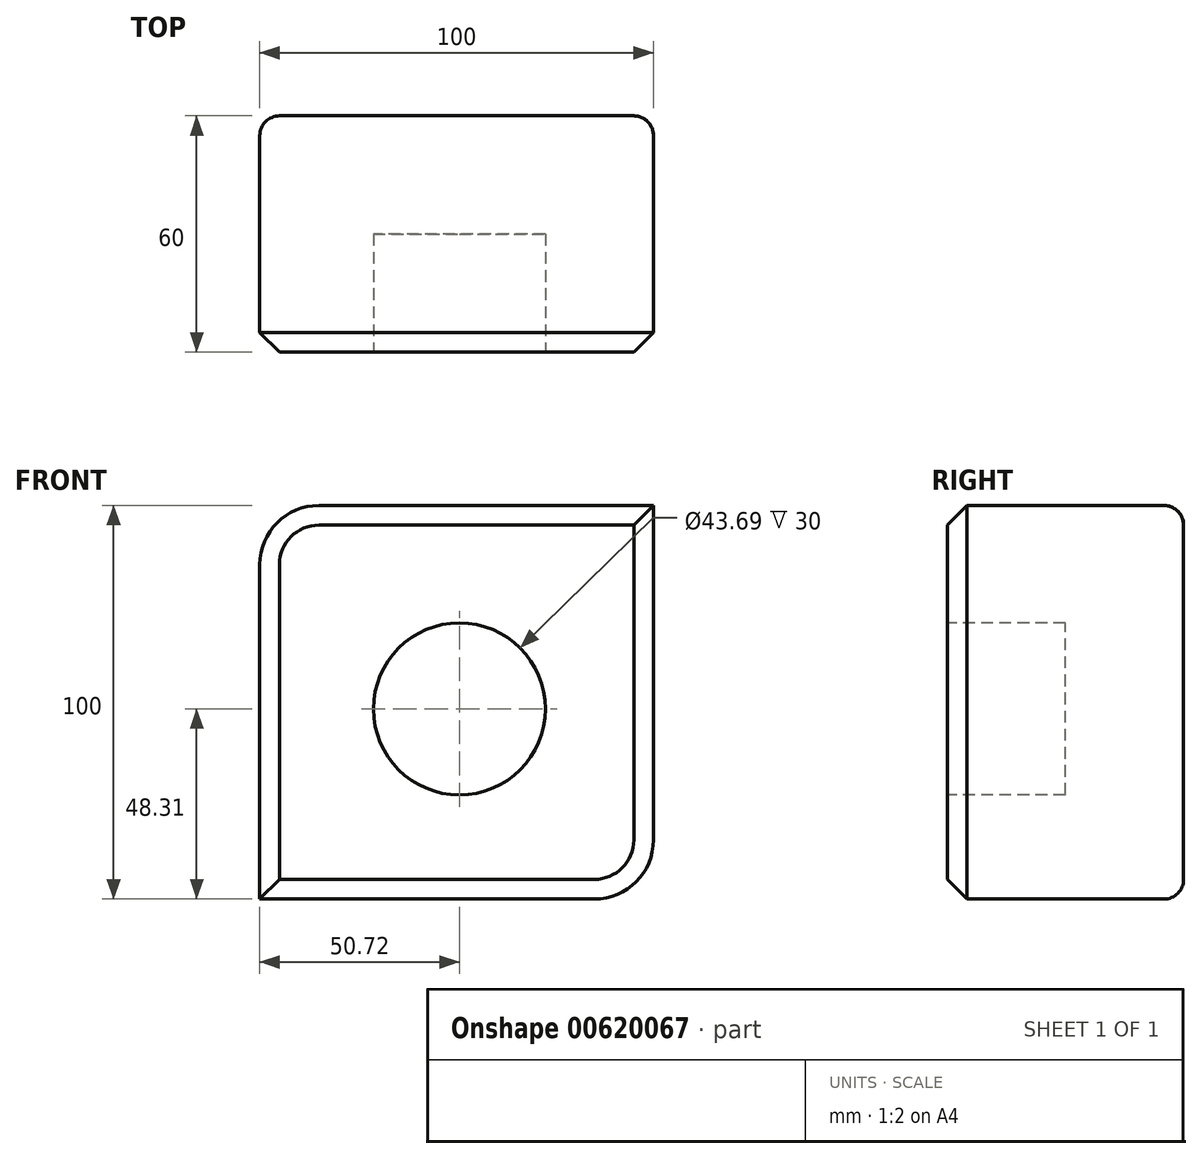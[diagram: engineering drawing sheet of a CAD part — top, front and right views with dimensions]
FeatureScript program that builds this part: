
annotation { "Feature Type Name" : "Feature", "Feature Type Description" : "" }
export const myFeature = defineFeature(function(context is Context, id is Id, definition is map)
    precondition{}
    {
        {
            var Q0;
            Q0=qCreatedBy(makeId("Front.planeOp"),FACE);
            var sketch = newSketch(context, id + "F0", { "sketchPlane" : qUnion([Q0])});
            skLineSegment(sketch, "E0.bottom", {"start": v(-35.72, 51.7) * mm, "end": v(49.28, 51.7) * mm});
            skLineSegment(sketch, "E0.top", {"start": v(-50.72, -48.3) * mm, "end": v(34.28, -48.3) * mm});
            skLineSegment(sketch, "E0.left", {"start": v(-50.72, 36.7) * mm, "end": v(-50.72, -48.3) * mm});
            skLineSegment(sketch, "E0.right", {"start": v(49.28, 51.7) * mm, "end": v(49.28, -33.3) * mm});
            skPoint(sketch, "E1.visualSharp", {"position": v(-50.72, 51.7) * mm});
            skArc(sketch, "E1.filletArc", {"start": v(-35.72, 51.7) * mm, "mid": v(-46.32, 47.3) * mm, "end": v(-50.72, 36.7) * mm});
            skPoint(sketch, "E2.visualSharp", {"position": v(49.28, -48.3) * mm});
            skArc(sketch, "E2.filletArc", {"start": v(34.28, -48.3) * mm, "mid": v(44.89, -43.91) * mm, "end": v(49.28, -33.3) * mm});
            skSolve(sketch);
        }
        {
            var Q0;
            Q0 = qSketchRegion(id + "F0", true);
            extrude(context, id + "F1", {"entities" : qUnion([Q0]), "depth" : 60 * mm, "offsetDistance" : 25 * mm});
        }
        {
            var Q0;
            Q0=makeQuery(id+"F1.opExtrude","CAP_FACE",FACE,{"disambiguationData":[OSD([sQuery(id+"F0.wireOp",EDGE,"E0.bottom"),sQuery(id+"F0.wireOp",EDGE,"E0.top"),sQuery(id+"F0.wireOp",EDGE,"E0.left"),sQuery(id+"F0.wireOp",EDGE,"E0.right"),sQuery(id+"F0.wireOp",EDGE,"E1.filletArc"),sQuery(id+"F0.wireOp",EDGE,"E2.filletArc")])],"isStart":true});
            fillet(context, id + "F2", {"entities" : qUnion([Q0]), "radius" : 5 * mm, "tangentPropagation" : true, "allowEdgeOverflow" : false});
        }
        {
            var Q0;
            Q0=makeQuery(id+"F1.opExtrude","CAP_FACE",FACE,{"disambiguationData":[OSD([sQuery(id+"F0.wireOp",EDGE,"E0.bottom"),sQuery(id+"F0.wireOp",EDGE,"E0.top"),sQuery(id+"F0.wireOp",EDGE,"E0.left"),sQuery(id+"F0.wireOp",EDGE,"E0.right"),sQuery(id+"F0.wireOp",EDGE,"E1.filletArc"),sQuery(id+"F0.wireOp",EDGE,"E2.filletArc")])],"isStart":false});
            chamfer(context, id + "F3", {"entities" : qUnion([Q0]), "width" : 5 * mm, "tangentPropagation" : true});
        }
        {
            var Q0;
            Q0=makeQuery(id+"F1.opExtrude","CAP_FACE",FACE,{"disambiguationData":[OSD([sQuery(id+"F0.wireOp",EDGE,"E0.bottom"),sQuery(id+"F0.wireOp",EDGE,"E0.top"),sQuery(id+"F0.wireOp",EDGE,"E0.left"),sQuery(id+"F0.wireOp",EDGE,"E0.right"),sQuery(id+"F0.wireOp",EDGE,"E1.filletArc"),sQuery(id+"F0.wireOp",EDGE,"E2.filletArc")])],"isStart":false});
            var sketch = newSketch(context, id + "F4", { "sketchPlane" : qUnion([Q0])});
            skSolve(sketch);
        }
        {
            var Q0;
            {var subQ0=sQuery(id+"F0.wireOp",EDGE,"E2.filletArc");var subQ1=sQuery(id+"F0.wireOp",EDGE,"E1.filletArc");var subQ2=sQuery(id+"F0.wireOp",EDGE,"E0.right");var subQ3=sQuery(id+"F0.wireOp",EDGE,"E0.left");var subQ4=sQuery(id+"F0.wireOp",EDGE,"E0.top");var subQ5=sQuery(id+"F0.wireOp",EDGE,"E0.bottom");var subQ6=makeQuery(id+"F1.opExtrude","CAP_FACE",FACE,{"disambiguationData":[OSD([subQ5,subQ4,subQ3,subQ2,subQ1,subQ0])],"isStart":false});Q0=makeQuery(id+"F4.imprint","IMPRINT",FACE,{"disambiguationData":[TD([[makeQuery(id+"F4.imprint","IMPRINT",EDGE,{"derivedFrom":makeQuery(id+"F3.opChamfer","BLEND_EDGE",EDGE,{"blendedFrom":[makeQuery(id+"F1.opExtrude","CAP_EDGE",EDGE,{"disambiguationData":[OSD([subQ5])],"isStart":false}),subQ6],"blendedInto":[subQ6]})}),1.0]])]});}
            var sketch = newSketch(context, id + "F5", { "sketchPlane" : qUnion([Q0])});
            skCircle(sketch, "E3", {"center": v(0, 0) * mm, "radius": 21.85 * mm});
            skSolve(sketch);
        }
        {
            var Q0;
            Q0 = qSketchRegion(id + "F5", true);
            extrude(context, id + "F6", {"entities" : qUnion([Q0]), "operationType" : NewBodyOperationType.REMOVE, "oppositeDirection" : true, "depth" : 30 * mm, "offsetDistance" : 25 * mm});
        }
    });
